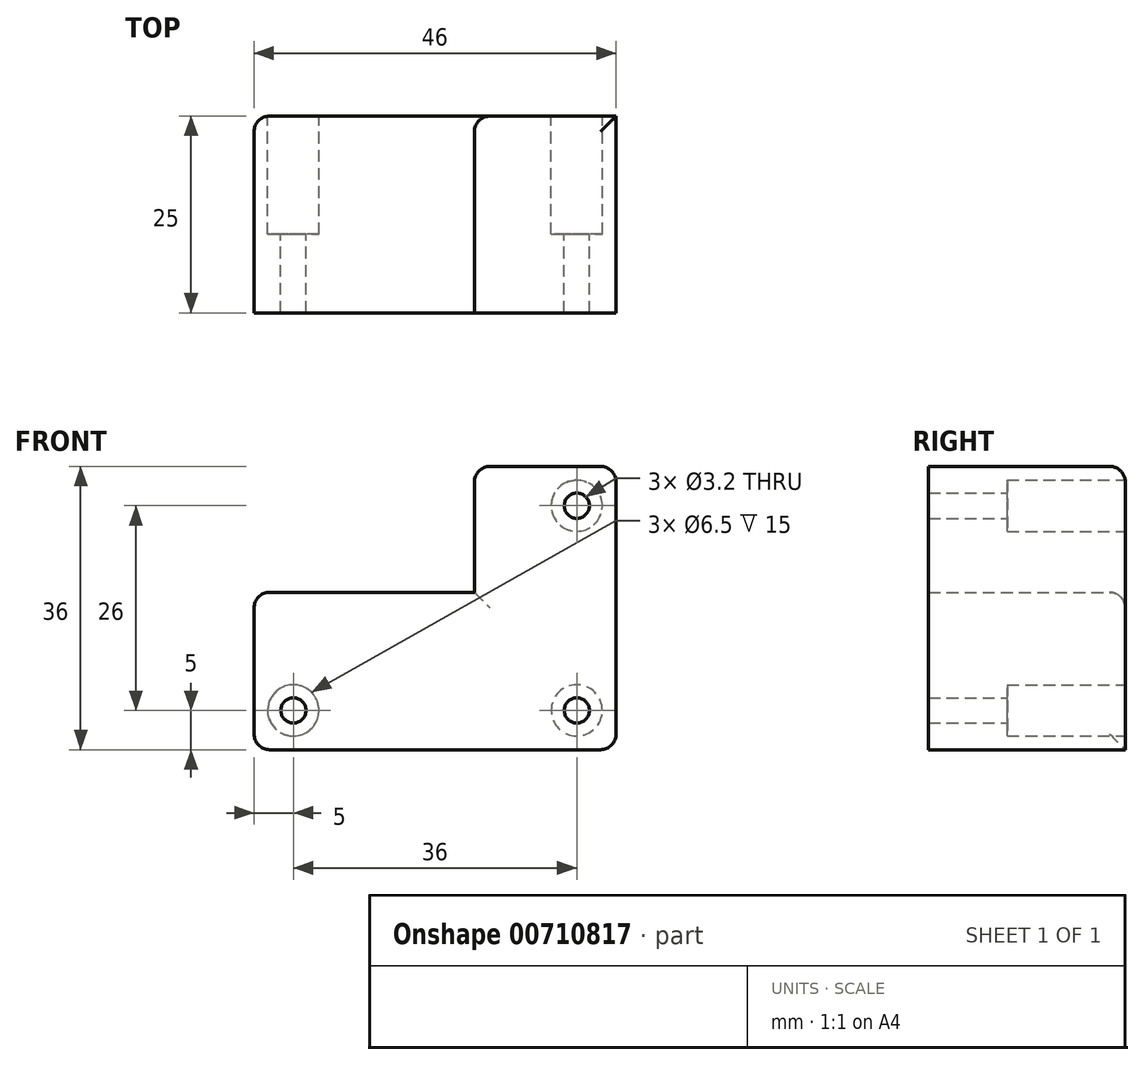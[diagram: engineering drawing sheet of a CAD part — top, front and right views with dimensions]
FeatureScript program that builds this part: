
annotation { "Feature Type Name" : "Feature", "Feature Type Description" : "" }
export const myFeature = defineFeature(function(context is Context, id is Id, definition is map)
    precondition{}
    {
        {
            var Q0;
            Q0=qCreatedBy(makeId("Front.planeOp"),FACE);
            var sketch = newSketch(context, id + "F0", { "sketchPlane" : qUnion([Q0])});
            skPoint(sketch, "E0.middle", {"position": v(0, 0) * mm});
            skLineSegment(sketch, "E1.bottom", {"start": v(-23, -18) * mm, "end": v(23, -18) * mm});
            skLineSegment(sketch, "E1.top", {"start": v(-23, 18) * mm, "end": v(23, 18) * mm});
            skLineSegment(sketch, "E1.left", {"start": v(-23, -18) * mm, "end": v(-23, 18) * mm});
            skLineSegment(sketch, "E1.right", {"start": v(23, -18) * mm, "end": v(23, 18) * mm});
            skLineSegment(sketch, "E2.bottom", {"start": v(-23, 0) * mm, "end": v(3, 0) * mm});
            skLineSegment(sketch, "E2.top", {"start": v(-23, 18) * mm, "end": v(3, 18) * mm});
            skLineSegment(sketch, "E2.left", {"start": v(-23, 0) * mm, "end": v(-23, 18) * mm});
            skLineSegment(sketch, "E2.right", {"start": v(3, 0) * mm, "end": v(3, 18) * mm});
            skCircle(sketch, "E3", {"center": v(-18, -13) * mm, "radius": 1.6 * mm});
            skCircle(sketch, "E4", {"center": v(18, -13) * mm, "radius": 1.6 * mm});
            skCircle(sketch, "E5", {"center": v(18, 13) * mm, "radius": 1.6 * mm});
            skCircle(sketch, "E6", {"center": v(18, 13) * mm, "radius": 3.25 * mm});
            skCircle(sketch, "E7", {"center": v(18, -13) * mm, "radius": 3.25 * mm});
            skCircle(sketch, "E8", {"center": v(-18, -13) * mm, "radius": 3.25 * mm});
            skLineSegment(sketch, "E9", {"start": v(-23, 2) * mm, "end": v(3, 2) * mm});
            skLineSegment(sketch, "E10", {"start": v(3, 2) * mm, "end": v(5, 2) * mm});
            skLineSegment(sketch, "E11", {"start": v(5, 2) * mm, "end": v(5, 18) * mm});
            skSolve(sketch);
        }
        {
            var Q0;
            Q0=makeQuery(id+"F0.imprint","IMPRINT",FACE,{"disambiguationData":[TD([[makeQuery(id+"F0.imprint","IMPRINT",EDGE,{"derivedFrom":sQuery(id+"F0.wireOp",EDGE,"E1.bottom")}),1.0]])]});
            var Q1;
            Q1=makeQuery(id+"F0.imprint","IMPRINT",FACE,{"disambiguationData":[TD([[makeQuery(id+"F0.imprint","IMPRINT",EDGE,{"derivedFrom":sQuery(id+"F0.wireOp",EDGE,"E5")}),-1.0]])]});
            var Q2;
            Q2=makeQuery(id+"F0.imprint","IMPRINT",FACE,{"disambiguationData":[TD([[makeQuery(id+"F0.imprint","IMPRINT",EDGE,{"derivedFrom":sQuery(id+"F0.wireOp",EDGE,"E4")}),-1.0]])]});
            var Q3;
            Q3=makeQuery(id+"F0.imprint","IMPRINT",FACE,{"disambiguationData":[TD([[makeQuery(id+"F0.imprint","IMPRINT",EDGE,{"derivedFrom":sQuery(id+"F0.wireOp",EDGE,"E3")}),-1.0]])]});
            var Q4;
            {var subQ0=sQuery(id+"F0.wireOp",EDGE,"E2.bottom");Q4=makeQuery(id+"F0.imprint","IMPRINT",FACE,{"disambiguationData":[TD([[makeQuery(id+"F0.imprint","IMPRINT",EDGE,{"derivedFrom":subQ0}),1.0]])]});}
            extrude(context, id + "F1", {"entities" : qUnion([Q0, Q1, Q2, Q3, Q4]), "depth" : 25 * mm, "offsetDistance" : 25 * mm});
        }
        {
            var Q0;
            Q0=makeQuery(id+"F0.imprint","IMPRINT",FACE,{"disambiguationData":[TD([[makeQuery(id+"F0.imprint","IMPRINT",EDGE,{"derivedFrom":sQuery(id+"F0.wireOp",EDGE,"E4")}),-1.0]])]});
            var Q1;
            Q1=makeQuery(id+"F0.imprint","IMPRINT",FACE,{"disambiguationData":[TD([[makeQuery(id+"F0.imprint","IMPRINT",EDGE,{"derivedFrom":sQuery(id+"F0.wireOp",EDGE,"E3")}),-1.0]])]});
            var Q2;
            Q2=makeQuery(id+"F0.imprint","IMPRINT",FACE,{"disambiguationData":[TD([[makeQuery(id+"F0.imprint","IMPRINT",EDGE,{"derivedFrom":sQuery(id+"F0.wireOp",EDGE,"E5")}),-1.0]])]});
            extrude(context, id + "F2", {"entities" : qUnion([Q0, Q1, Q2]), "operationType" : NewBodyOperationType.REMOVE, "depth" : 15 * mm, "offsetDistance" : 25 * mm});
        }
        {
            var Q0;
            Q0=makeQuery(id+"F1.opExtrude","CAP_EDGE",EDGE,{"disambiguationData":[OSD([sQuery(id+"F0.wireOp",EDGE,"E1.left")])],"isStart":true});
            var Q1;
            Q1=makeQuery(id+"F1.opExtrude","CAP_EDGE",EDGE,{"disambiguationData":[OSD([sQuery(id+"F0.wireOp",EDGE,"E2.bottom")])],"isStart":true});
            var Q2;
            Q2=makeQuery(id+"F1.opExtrude","CAP_EDGE",EDGE,{"disambiguationData":[OSD([sQuery(id+"F0.wireOp",EDGE,"E2.right")])],"isStart":true});
            var Q3;
            Q3=makeQuery(id+"F1.opExtrude","CAP_EDGE",EDGE,{"disambiguationData":[OSD([sQuery(id+"F0.wireOp",EDGE,"E1.top")])],"isStart":true});
            var Q4;
            Q4=makeQuery(id+"F1.opExtrude","SWEPT_EDGE",EDGE,{"disambiguationData":[OSD([sQuery(id+"F0.wireOp",EDGE,"E1.left"),sQuery(id+"F0.wireOp",EDGE,"E2.bottom"),sQuery(id+"F0.wireOp",EDGE,"E2.left")])]});
            var Q5;
            Q5=makeQuery(id+"F1.opExtrude","SWEPT_EDGE",EDGE,{"disambiguationData":[OSD([sQuery(id+"F0.wireOp",EDGE,"E1.top"),sQuery(id+"F0.wireOp",EDGE,"E2.top"),sQuery(id+"F0.wireOp",EDGE,"E2.right")])]});
            var Q6;
            Q6=makeQuery(id+"F1.opExtrude","SWEPT_EDGE",EDGE,{"disambiguationData":[OSD([sQuery(id+"F0.wireOp",EDGE,"E1.bottom"),sQuery(id+"F0.wireOp",EDGE,"E1.left")])]});
            var Q7;
            Q7=makeQuery(id+"F1.opExtrude","SWEPT_EDGE",EDGE,{"disambiguationData":[OSD([sQuery(id+"F0.wireOp",EDGE,"E1.bottom"),sQuery(id+"F0.wireOp",EDGE,"E1.right")])]});
            var Q8;
            Q8=makeQuery(id+"F1.opExtrude","SWEPT_EDGE",EDGE,{"disambiguationData":[OSD([sQuery(id+"F0.wireOp",EDGE,"E1.top"),sQuery(id+"F0.wireOp",EDGE,"E1.right")])]});
            var Q9;
            Q9=makeQuery(id+"F1.opExtrude","CAP_EDGE",EDGE,{"disambiguationData":[OSD([sQuery(id+"F0.wireOp",EDGE,"E9")])],"isStart":true});
            var Q10;
            Q10=makeQuery(id+"F1.opExtrude","CAP_EDGE",EDGE,{"disambiguationData":[OSD([sQuery(id+"F0.wireOp",EDGE,"E11")])],"isStart":true});
            fillet(context, id + "F3", {"entities" : qUnion([Q0, Q1, Q2, Q3, Q4, Q5, Q6, Q7, Q8, Q9, Q10]), "radius" : 2 * mm, "tangentPropagation" : true, "allowEdgeOverflow" : false});
        }
    });
